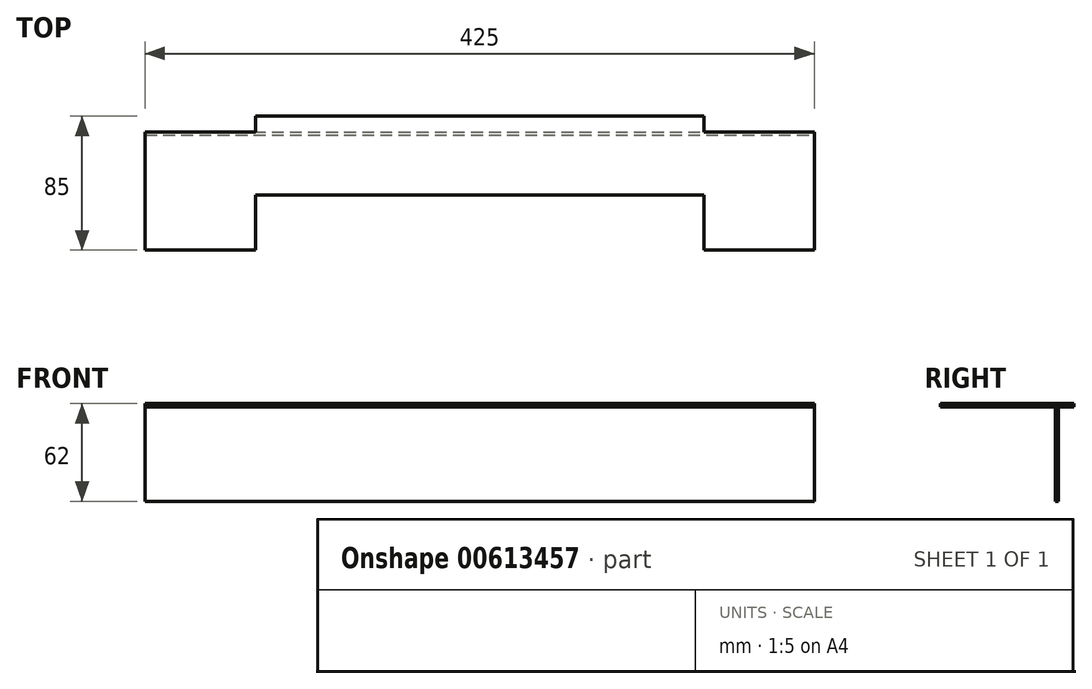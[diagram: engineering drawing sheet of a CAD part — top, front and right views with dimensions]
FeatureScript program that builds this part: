
annotation { "Feature Type Name" : "Feature", "Feature Type Description" : "" }
export const myFeature = defineFeature(function(context is Context, id is Id, definition is map)
    precondition{}
    {
        {
            var Q0;
            Q0=qCreatedBy(makeId("Top.planeOp"),FACE);
            var sketch = newSketch(context, id + "F0", { "sketchPlane" : qUnion([Q0])});
            skLineSegment(sketch, "E0.top", {"start": v(-142.5, 0) * mm, "end": v(142.5, 0) * mm});
            skPoint(sketch, "E1", {"position": v(0, 0) * mm});
            skLineSegment(sketch, "E2.top", {"start": v(-212.5, -85) * mm, "end": v(-142.5, -85) * mm});
            skLineSegment(sketch, "E2.left", {"start": v(-212.5, -10) * mm, "end": v(-212.5, -85) * mm});
            skLineSegment(sketch, "E2.right", {"start": v(212.5, -10) * mm, "end": v(212.5, -85) * mm});
            skLineSegment(sketch, "E3", {"start": v(-142.5, 0) * mm, "end": v(-142.5, -85) * mm, "construction": true});
            skLineSegment(sketch, "E4", {"start": v(142.5, 0) * mm, "end": v(142.5, -85) * mm, "construction": true});
            skLineSegment(sketch, "E5.top", {"start": v(-142.5, -10) * mm, "end": v(142.5, -10) * mm});
            skLineSegment(sketch, "E5.left", {"start": v(-142.5, -85) * mm, "end": v(-142.5, -10) * mm});
            skLineSegment(sketch, "E5.right", {"start": v(142.5, -85) * mm, "end": v(142.5, -10) * mm});
            skPoint(sketch, "E6", {"position": v(0, -10) * mm});
            skLineSegment(sketch, "E7.top", {"start": v(-142.5, -50) * mm, "end": v(142.5, -50) * mm});
            skLineSegment(sketch, "E7.left", {"start": v(-142.5, -10) * mm, "end": v(-142.5, -50) * mm});
            skLineSegment(sketch, "E7.right", {"start": v(142.5, -10) * mm, "end": v(142.5, -50) * mm});
            skLineSegment(sketch, "E8", {"start": v(-142.5, 0) * mm, "end": v(-142.5, -10) * mm});
            skLineSegment(sketch, "E9", {"start": v(142.5, 0) * mm, "end": v(142.5, -10) * mm});
            skLineSegment(sketch, "E10", {"start": v(-142.5, -10) * mm, "end": v(-212.5, -10) * mm});
            skLineSegment(sketch, "E11", {"start": v(142.5, -10) * mm, "end": v(212.5, -10) * mm});
            skLineSegment(sketch, "E12.trimOffspring", {"start": v(142.5, -85) * mm, "end": v(212.5, -85) * mm});
            skPoint(sketch, "E13.orphan", {"position": v(-212.5, 0) * mm});
            skPoint(sketch, "E14.orphan", {"position": v(212.5, 0) * mm});
            skSolve(sketch);
        }
        {
            var Q0;
            {var subQ3=sQuery(id+"F0.wireOp",EDGE,"E5.left");Q0=makeQuery(id+"F0.imprint","IMPRINT",FACE,{"disambiguationData":[TD([[makeQuery(id+"F0.imprint","IMPRINT",EDGE,{"derivedFrom":subQ3}),1.0]])]});}
            var Q1;
            Q1=makeQuery(id+"F0.imprint","IMPRINT",FACE,{"disambiguationData":[TD([[makeQuery(id+"F0.imprint","IMPRINT",EDGE,{"derivedFrom":sQuery(id+"F0.wireOp",EDGE,"E5.top")}),-1.0]])]});
            var Q2;
            Q2=makeQuery(id+"F0.imprint","IMPRINT",FACE,{"disambiguationData":[TD([[makeQuery(id+"F0.imprint","IMPRINT",EDGE,{"derivedFrom":sQuery(id+"F0.wireOp",EDGE,"E5.top")}),1.0]])]});
            var Q3;
            {var subQ3=sQuery(id+"F0.wireOp",EDGE,"E5.right");Q3=makeQuery(id+"F0.imprint","IMPRINT",FACE,{"disambiguationData":[TD([[makeQuery(id+"F0.imprint","IMPRINT",EDGE,{"derivedFrom":subQ3}),-1.0]])]});}
            extrude(context, id + "F1", {"entities" : qUnion([Q0, Q1, Q2, Q3]), "depth" : 2 * mm, "offsetDistance" : 25 * mm});
        }
        {
            var Q0;
            Q0=qCreatedBy(makeId("Front.planeOp"),FACE);
            cPlane(context, id + "F2", {"entities" : qUnion([Q0]), "cplaneType" : CPlaneType.OFFSET, "offset" : 10 * mm, "width" : 150 * mm, "height" : 150 * mm});
        }
        {
            var Q0;
            Q0=qCreatedBy(id+"F2.planeOp",FACE);
            var sketch = newSketch(context, id + "F3", { "sketchPlane" : qUnion([Q0])});
            skLineSegment(sketch, "E15.bottom", {"start": v(-212.5, 0) * mm, "end": v(212.5, 0) * mm});
            skLineSegment(sketch, "E15.top", {"start": v(-212.5, -60) * mm, "end": v(212.5, -60) * mm});
            skLineSegment(sketch, "E15.left", {"start": v(-212.5, 0) * mm, "end": v(-212.5, -60) * mm});
            skLineSegment(sketch, "E15.right", {"start": v(212.5, 0) * mm, "end": v(212.5, -60) * mm});
            skSolve(sketch);
        }
        {
            var Q0;
            Q0=makeQuery(id+"F3.imprint","IMPRINT",FACE,{"disambiguationData":[TD([[makeQuery(id+"F3.imprint","IMPRINT",EDGE,{"derivedFrom":sQuery(id+"F3.wireOp",EDGE,"E15.bottom")}),-1.0]])]});
            extrude(context, id + "F4", {"entities" : qUnion([Q0]), "depth" : 2 * mm, "offsetDistance" : 25 * mm});
        }
    });
